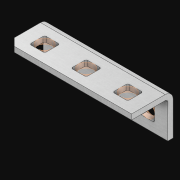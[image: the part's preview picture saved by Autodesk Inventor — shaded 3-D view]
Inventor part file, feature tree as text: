
AUTODESK INVENTOR PART (.ipt)
format: ipt  version: 2021 (Build 250183000, 183)  size: 535,552 bytes
history: native  units: in
note: dims shown in document units (in); Inventor stores cm internally (conversion verified against a paired STEP export)
features: extrude x7, other x6, sketch x3, pattern_linear x1, sheet_metal_op x1
ambient origin geometry x8: Origin, YZ Plane, XZ Plane, XY Plane, X Axis, Y Axis, Z Axis, Center Point
bodies: Solid1 (feature_tree)
feature tree (18):
  pattern_linear  "Rectangular Pattern1"  Spacing1=0.063in  [1 undecoded]
  extrude  "Extrusion1"  Depth=0.5in
  sketch  "Sketch1"  dims[d0=0.182in]
  other  "Srf1"
  sketch  "Sketch2"  dims[d1=0.063in d2=0.0in]
  other  "Srf2"
  other  "Srf3"
  other  "Srf5"
  other  "Srf4"
  other  "Srf6"
  sketch  "Sketch3"  dims[d3=0.182in d4=0.063in d5=0.0in d8=0.5in d9=16.0in d10=0.0in]
  sheet_metal_op  "Fold1"
  extrude  "ExtrusionSrf1"  Depth=0.5in TaperAngle=0.0deg
  extrude  "ExtrusionSrf2"  [1 undecoded]
  extrude  "ExtrusionSrf3"  [1 undecoded]
  extrude  "ExtrusionSrf4"  [1 undecoded]
  extrude  "ExtrusionSrf37"  [1 undecoded]
  extrude  "ExtrusionSrf38"  [1 undecoded]
note: 6 required parameter values undecoded (feature->parameter linkage not recoverable at this tier; creation-order binding heuristic only, values carry confidence <= 0.55)
